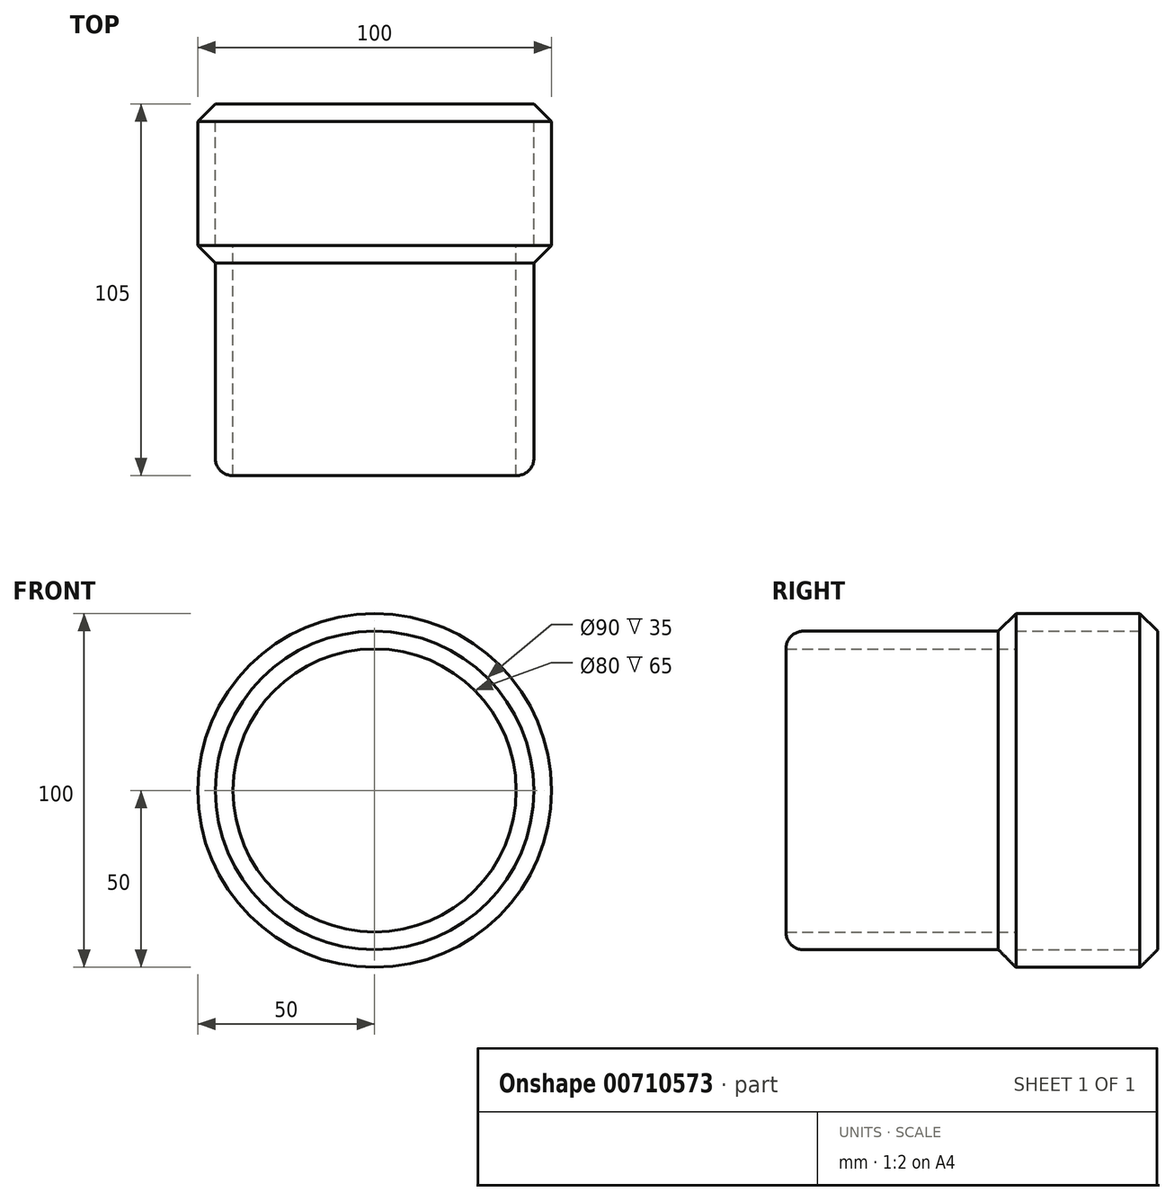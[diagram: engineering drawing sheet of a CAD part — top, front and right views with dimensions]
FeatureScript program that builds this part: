
annotation { "Feature Type Name" : "Feature", "Feature Type Description" : "" }
export const myFeature = defineFeature(function(context is Context, id is Id, definition is map)
    precondition{}
    {
        {
            var Q0;
            Q0=qCreatedBy(makeId("Front.planeOp"),FACE);
            var sketch = newSketch(context, id + "F0", { "sketchPlane" : qUnion([Q0])});
            skCircle(sketch, "E0", {"center": v(0, 0) * mm, "radius": 50 * mm});
            skSolve(sketch);
        }
        {
            var Q0;
            Q0=makeQuery(id+"F0.imprint","IMPRINT",FACE,{"disambiguationData":[TD([[makeQuery(id+"F0.imprint","IMPRINT",EDGE,{"derivedFrom":sQuery(id+"F0.wireOp",EDGE,"E0")}),1.0]])]});
            extrude(context, id + "F1", {"entities" : qUnion([Q0]), "depth" : 45 * mm, "offsetDistance" : 25 * mm});
        }
        {
            var Q0;
            Q0=makeQuery(id+"F1.opExtrude","CAP_FACE",FACE,{"disambiguationData":[OSD([sQuery(id+"F0.wireOp",EDGE,"E0")])],"isStart":false});
            shell(context, id + "F2", {"entities" : qUnion([Q0]), "thickness" : 5 * mm});
        }
        {
            var Q0;
            {var subQ0=sQuery(id+"F0.wireOp",EDGE,"E0");Q0=makeQuery(id+"F2.opShell","OFFSET_FACE",FACE,{"disambiguationData":[OSD([subQ0]),TDD([makeQuery(id+"F1.opExtrude","CAP_FACE",FACE,{"disambiguationData":[OSD([subQ0])],"isStart":true})])]});}
            extrude(context, id + "F3", {"entities" : qUnion([Q0]), "operationType" : NewBodyOperationType.ADD, "depth" : 100 * mm, "offsetDistance" : 25 * mm});
        }
        {
            var Q0;
            Q0=makeQuery(id+"F3.opExtrude","CAP_FACE",FACE,{"disambiguationData":[OSD([sQuery(id+"F0.wireOp",EDGE,"E0")])],"isStart":false});
            fillet(context, id + "F4", {"entities" : qUnion([Q0]), "radius" : 4.83 * mm, "tangentPropagation" : true, "allowEdgeOverflow" : false});
        }
        {
            var Q0;
            Q0=makeQuery(id+"F3.opExtrude","CAP_FACE",FACE,{"disambiguationData":[OSD([sQuery(id+"F0.wireOp",EDGE,"E0")])],"isStart":false});
            shell(context, id + "F5", {"entities" : qUnion([Q0]), "thickness" : 5 * mm});
        }
        {
            var Q0;
            Q0=makeQuery(id+"F1.opExtrude","SWEPT_FACE",FACE,{"disambiguationData":[OSD([sQuery(id+"F0.wireOp",EDGE,"E0")])]});
            chamfer(context, id + "F6", {"entities" : qUnion([Q0]), "width" : 5 * mm, "tangentPropagation" : true});
        }
    });
